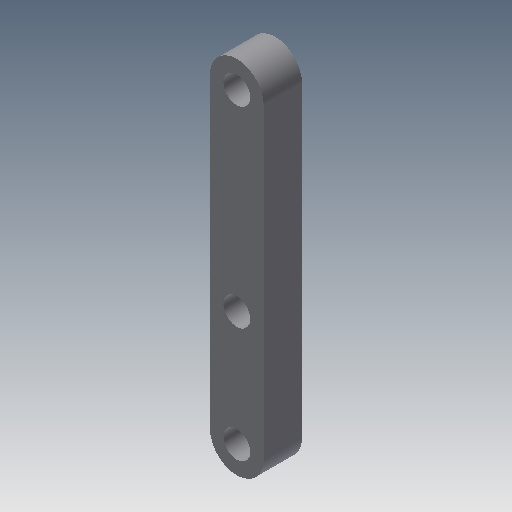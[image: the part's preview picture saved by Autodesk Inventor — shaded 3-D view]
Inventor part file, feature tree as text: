
AUTODESK INVENTOR PART (.ipt)
format: ipt  version: 2018 (Build 220112000, 112)  size: 105,984 bytes
history: native  units: mm
features: extrude x3, sketch x3
ambient origin geometry x8: Origin, YZ Plane, XZ Plane, XY Plane, X Axis, Y Axis, Z Axis, Center Point
bodies: Solid1 (feature_tree)
feature tree (6):
  extrude  "Extrusion1"  Depth=40.0mm
  extrude  "Extrusion2"  Depth=5.0mm TaperAngle=0.0deg
  extrude  "Extrusion3"  Depth=3.5mm
  sketch  "Sketch1"  dims[d0=7.0mm d1=40.0mm]
  sketch  "Sketch2"  dims[d2=7.0mm d3=5.0mm d4=0.0mm]
  sketch  "Sketch3"  dims[d5=3.5mm d6=3.5mm d7=5.0mm d8=0.0mm d9=15.0mm d10=3.5mm d11=10.0mm d12=0.0mm]
